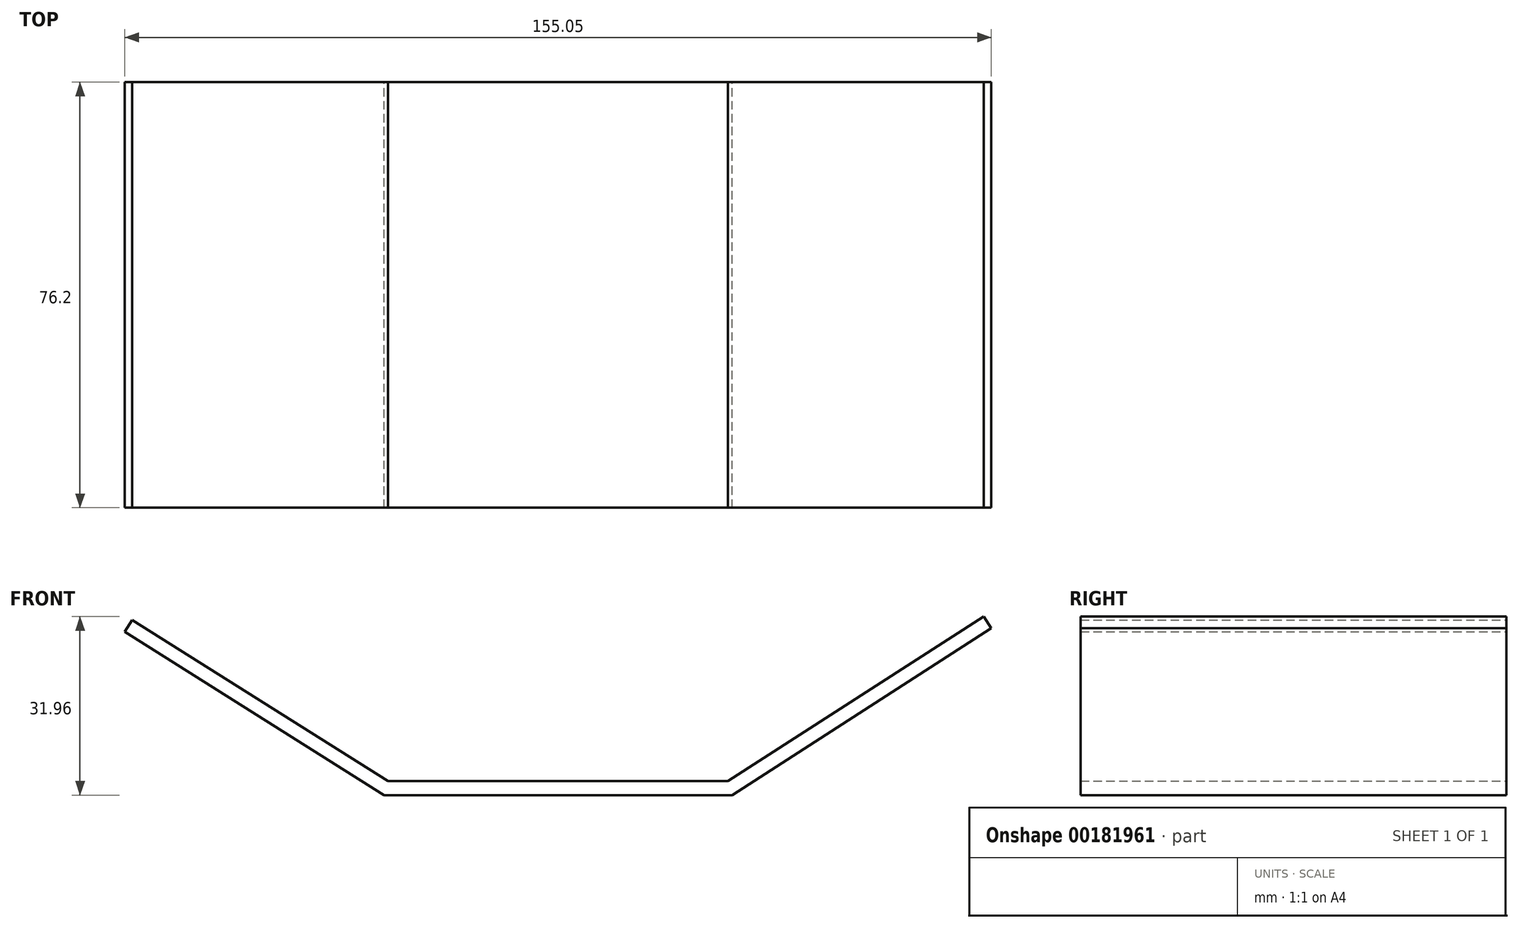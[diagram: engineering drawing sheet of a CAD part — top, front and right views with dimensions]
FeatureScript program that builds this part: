
annotation { "Feature Type Name" : "Feature", "Feature Type Description" : "" }
export const myFeature = defineFeature(function(context is Context, id is Id, definition is map)
    precondition{}
    {
        {
            var Q0;
            Q0=qCreatedBy(makeId("Front.planeOp"),FACE);
            var sketch = newSketch(context, id + "F0", { "sketchPlane" : qUnion([Q0])});
            skLineSegment(sketch, "E0", {"start": v(-30.3, 0) * mm, "end": v(30.52, 0) * mm});
            skLineSegment(sketch, "E1", {"start": v(30.52, 0) * mm, "end": v(-30.3, 0) * mm});
            skLineSegment(sketch, "E2", {"start": v(-30.3, 0) * mm, "end": v(-76.08, 28.84) * mm});
            skLineSegment(sketch, "E3", {"start": v(-76.08, 28.84) * mm, "end": v(-30.3, 0) * mm});
            skLineSegment(sketch, "E4", {"start": v(30.52, 0) * mm, "end": v(76.3, 29.47) * mm});
            skLineSegment(sketch, "E5.0", {"start": v(31.25, -2.49) * mm, "end": v(77.64, 27.38) * mm});
            skLineSegment(sketch, "E5.1", {"start": v(31.25, -2.49) * mm, "end": v(-31.03, -2.49) * mm});
            skLineSegment(sketch, "E5.2", {"start": v(-77.4, 26.74) * mm, "end": v(-31.03, -2.49) * mm});
            skLineSegment(sketch, "E6", {"start": v(-76.08, 28.84) * mm, "end": v(-77.4, 26.74) * mm});
            skLineSegment(sketch, "E7", {"start": v(76.3, 29.47) * mm, "end": v(77.64, 27.38) * mm});
            skSolve(sketch);
        }
        {
            var Q0;
            Q0=qSketchRegion(id+"F0",true);
            extrude(context, id + "F1", {"entities" : qUnion([Q0]), "depth" : 76.2 * mm});
        }
    });
